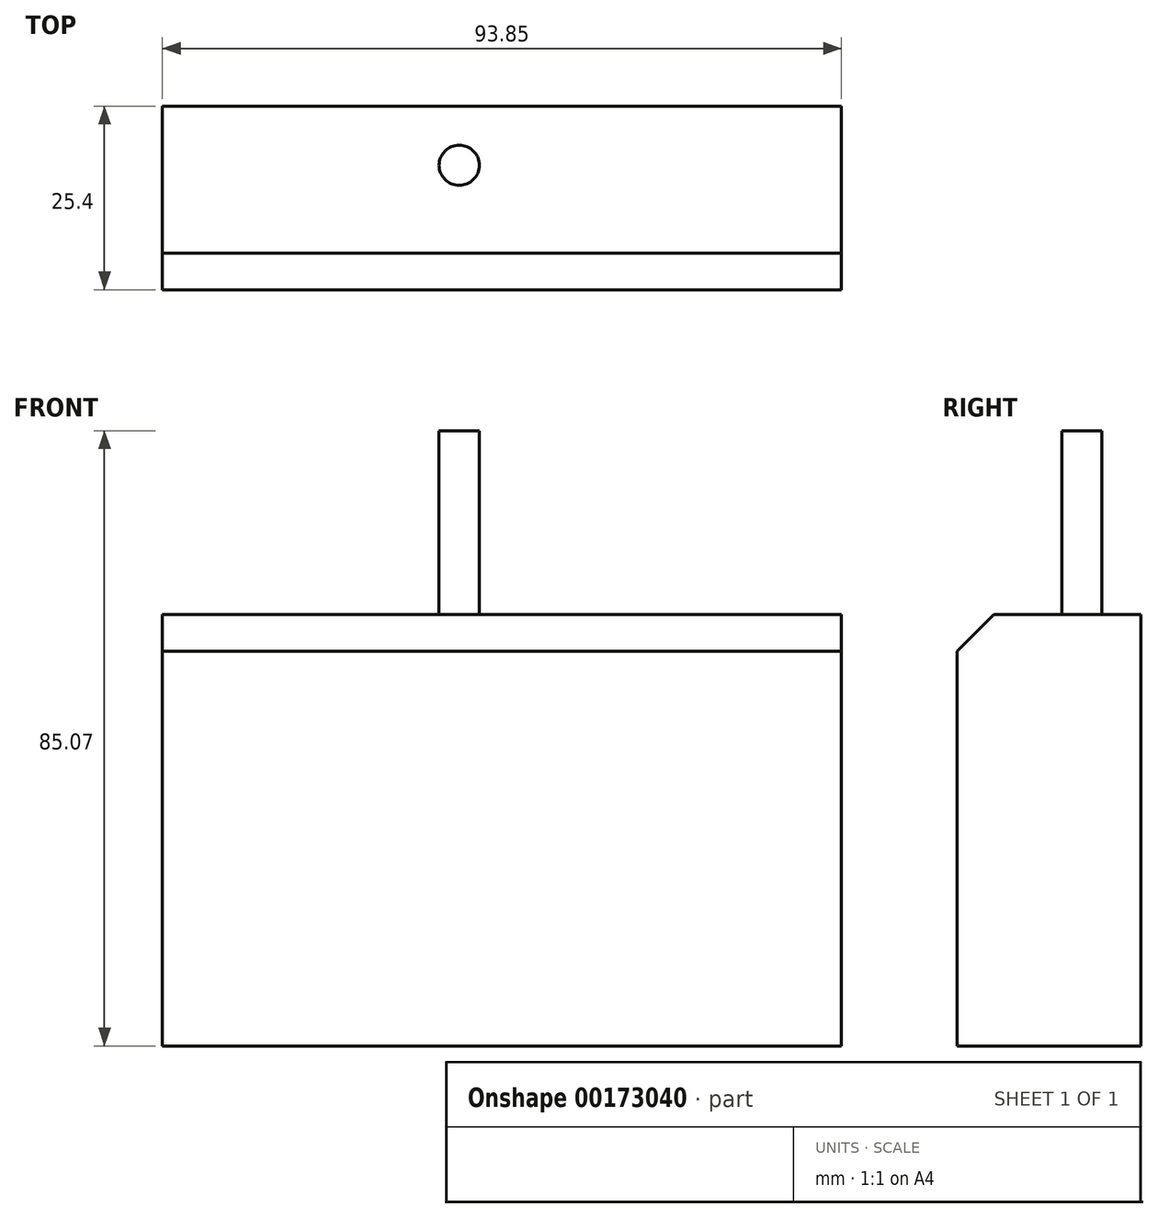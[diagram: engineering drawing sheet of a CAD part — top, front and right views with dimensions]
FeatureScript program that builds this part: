
annotation { "Feature Type Name" : "Feature", "Feature Type Description" : "" }
export const myFeature = defineFeature(function(context is Context, id is Id, definition is map)
    precondition{}
    {
        {
            var Q0;
            Q0=qCreatedBy(makeId("Front.planeOp"),FACE);
            var sketch = newSketch(context, id + "F0", { "sketchPlane" : qUnion([Q0])});
            skLineSegment(sketch, "E0.bottom", {"start": v(39.53, 29.65) * mm, "end": v(-54.32, 29.65) * mm});
            skLineSegment(sketch, "E0.top", {"start": v(39.53, -30.02) * mm, "end": v(-54.32, -30.02) * mm});
            skLineSegment(sketch, "E0.left", {"start": v(39.53, 29.65) * mm, "end": v(39.53, -30.02) * mm});
            skLineSegment(sketch, "E0.right", {"start": v(-54.32, 29.65) * mm, "end": v(-54.32, -30.02) * mm});
            skSolve(sketch);
        }
        {
            var Q0;
            Q0=makeQuery(id+"F0.imprint","IMPRINT",FACE,{"disambiguationData":[TD([[makeQuery(id+"F0.imprint","IMPRINT",EDGE,{"derivedFrom":sQuery(id+"F0.wireOp",EDGE,"E0.bottom")}),1.0]])]});
            extrude(context, id + "F1", {"entities" : qUnion([Q0]), "depth" : 25.4 * mm});
        }
        {
            var Q0;
            Q0=makeQuery(id+"F1.opExtrude","CAP_EDGE",EDGE,{"disambiguationData":[OSD([sQuery(id+"F0.wireOp",EDGE,"E0.bottom")])],"isStart":false});
            chamfer(context, id + "F2", {"entities" : qUnion([Q0]), "width" : 5.08 * mm, "tangentPropagation" : true});
        }
        {
            var Q0;
            Q0=makeQuery(id+"F1.opExtrude","SWEPT_FACE",FACE,{"disambiguationData":[OSD([sQuery(id+"F0.wireOp",EDGE,"E0.bottom")])]});
            var sketch = newSketch(context, id + "F3", { "sketchPlane" : qUnion([Q0])});
            skCircle(sketch, "E1", {"center": v(-13.3, -8.17) * mm, "radius": 2.78 * mm});
            skSolve(sketch);
        }
        {
            var Q0;
            Q0 = qSketchRegion(id + "F3", true);
            extrude(context, id + "F4", {"entities" : qUnion([Q0]), "operationType" : NewBodyOperationType.ADD, "depth" : 25.4 * mm});
        }
    });
